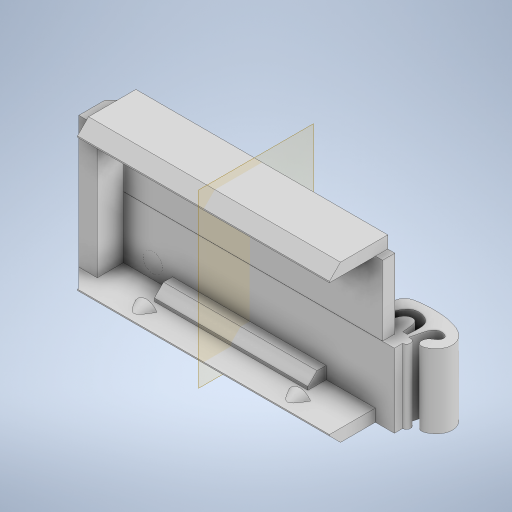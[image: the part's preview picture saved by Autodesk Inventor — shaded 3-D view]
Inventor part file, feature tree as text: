
AUTODESK INVENTOR PART (.ipt)
format: ipt  version: 2023 (Build 270158030, 158C)  size: 663,552 bytes
history: native  units: mm
features: extrude x12, other x6, sketch x6, chamfer x6, projected_geometry x6, plane x3, mirror x3, reference x1
ambient origin geometry x8: Origin, YZ Plane, XZ Plane, XY Plane, X Axis, Y Axis, Z Axis, Center Point
bodies: Solid1 (feature_tree)
feature tree (43):
  other  "Blocks"
  sketch  "Sketch1"  dims[d0=2.0mm d1=0.0mm d4=10.0mm d5=0.0mm]
  extrude  "Extrusion1"  Depth=10.0mm TaperAngle=0.0deg
  plane  "Work Plane1"
  extrude  "Extrusion2"  Depth=3.0mm
  mirror  "Mirror1"
  extrude  "Extrusion6"  Depth=17.780726mm
  extrude  "Extrusion16"  Depth=6.409146mm
  extrude  "Extrusion8"  Depth=1.257608mm
  mirror  "Mirror2"
  extrude  "Extrusion9"  Depth=10.0mm
  plane  "Work Plane10"
  extrude  "Extrusion11"  Depth=10.0mm
  extrude  "Extrusion12"  Depth=10.0mm
  mirror  "Mirror3"
  extrude  "Extrusion13"  Depth=10.0mm
  chamfer  "Chamfer5"  [1 undecoded]
  chamfer  "Chamfer6"  Distance=2.0mm
  chamfer  "Chamfer7"  Distance=10.0mm
  plane  "Work Plane5"
  extrude  "Extrusion14"  Depth=1.3mm
  extrude  "Extrusion15"  Depth=10.0mm
  chamfer  "Chamfer9"  Distance=12.0mm
  chamfer  "Chamfer10"  Distance=12.0mm
  chamfer  "Chamfer11"  [1 undecoded]
  extrude  "Extrusion17"  Depth=2.0mm TaperAngle=45.0deg
  reference  "Reference1"
  other  "DIN-rail-mount"
  sketch  "Sketch9"  dims[d41=23.55mm d43=3.0mm]
  sketch  "Sketch13"  dims[d44=0.4mm d45=17.780726mm]
  sketch  "Sketch14"  dims[d46=4.630585mm d47=6.409146mm]
  sketch  "Sketch15"  dims[d48=0.917895mm d49=1.257608mm]
  other  "board"
  projected_geometry  "Projected Loop11"
  projected_geometry  "Projected Loop12"
  projected_geometry  "Projected Loop13"
  projected_geometry  "Projected Loop14"
  projected_geometry  "Projected Loop15"
  sketch  "Sketch17"  dims[d50=1.6mm d51=0.803745mm d52=2.954284mm d53=0.7465mm d54=0.5mm d55=0.0mm d56=0.0mm d61=2.0mm d62=0.0mm d65=10.0mm d66=0.0mm d67=1.3mm d76=4.0mm d78=12.0mm d79=-4.537856mm d80=12.0mm d81=0.0mm d82=0.0mm d83=0.0mm d84=1.8mm d85=2.0mm d86=45.0deg d88=1.5mm d89=2.0mm d90=45.0deg d91=1.5mm d92=2.0mm d93=45.0deg d97=21.0mm d98=43.0mm d99=1.3mm d100=0.0mm d101=1.3mm d102=0.0mm d103=3.0mm d104=2.0mm d105=45.0deg d106=2.0mm d107=2.0mm d108=45.0deg d109=1.95mm d110=2.0mm d111=45.0deg d117=3.0mm d123=16.819631mm d124=17.830248mm d125=16.711144mm d126=0.704136mm d127=16.322468mm d129=4.370885mm d130=0.289941mm d131=0.003807mm d132=18.518058mm d133=20.70572mm d137=23.48774mm d138=0.990364mm d150=41.0mm d151=3.0mm d152=3.1mm d154=2.0mm d155=0.0mm d156=8.0mm d157=8.0mm d158=3.0mm d159=1.3mm d164=8.0mm d165=8.0mm d166=4.3mm d167=0.1mm d168=2.030384mm d169=10.0mm d170=0.0mm]
  projected_geometry  "Projected Loop16"
  other  "buck-converter-din-rail-mount.iam"
  other  "Power Buck Converter:1"
  other  "DIN-rail-mount:1"
note: 2 required parameter values undecoded (feature->parameter linkage not recoverable at this tier; creation-order binding heuristic only, values carry confidence <= 0.55)
